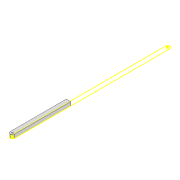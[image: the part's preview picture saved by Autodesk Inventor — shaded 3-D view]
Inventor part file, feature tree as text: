
AUTODESK INVENTOR PART (.ipt)
format: ipt  version: 2022 (Build 260153000, 153)  size: 103,936 bytes
history: native  units: mm
features: sketch x3, extrude x2, projected_geometry x1
ambient origin geometry x8: Origin, YZ Plane, XZ Plane, XY Plane, X Axis, Y Axis, Z Axis, Center Point
bodies: Solid1 (feature_tree)
feature tree (6):
  extrude  "Extrusion1"  Depth=10.0mm
  sketch  "Sketch2"  dims[d2=3.0mm d3=3.0mm]
  extrude  "Extrusion2"  Depth=3.0mm
  sketch  "Sketch1"  dims[d0=351.981mm d1=10.0mm]
  projected_geometry  "Projected Loop1"
  sketch  "Sketch3"  dims[d4=8.0mm d5=0.0mm d12=10.0mm d13=0.0mm]
